# Revit family: led-e-g45-fila-e27-2_8w-dim-2700k-fr_500010000800_a218
name_source: partatom
category: Leuchten
revit_build: Autodesk Revit 2016 (Build: 20190508_0715(x64)
units: mm (PartAtom-declared; Revit-internal decimal feet)

## family parameters
Basisbauteil = Fläche
Beim Laden mit Abzugskörper schneiden = Nein
Bemaßung runder Anschluss = Durchmesser verwenden
Gemeinsam genutzt = Nein
Lichtquelle = Nein
Raumberechnungspunkt = Nein
Teiletyp = Normal

## types (1)
- LED-E-G45-FILA-E27-2.8W-DIM-2700K-FR (1 x LED, 235 lm)
    Approval mark = CE
    Beschreibung = Classic light bulb shape ensures an easy replacement. Instant 100% light when switched on and no startup time. No UV / IR radiance so there is less risk of damage. Up to 86% less energy consumption than traditional bulbs.
    CIE Flux Codes = 21 45 72 54 99
    Height = 77 mm
    Hersteller = OPPLE
    Lamp Light Flux = 235 lm
    Lamp count = 1
    Lampe = 1 x LED
    Length = 45 mm
    Luminous efficacy = 83 lm/W
    ModVariant = Nein
    Modell = 500010000800
    Mounting Place = Ceiling
    Mounting Type = Surface mounted
    Number of Poles = 1
    OnlyDefault = Ja
    Power Factor = 1
    Product Name = LED-E-G45-FILA-E27-2.8W-DIM-2700K-FR
    Product group = Filament Mini Globe
    ProductGroupID = 312
    Protection Class = Protection class I
    Protection Degree = IP 20
    RLX_Detail_Level = 1
    RlxData = <blob elided: 15901 chars, md5=775f46ca>
    Scheinlast = 3 VA
    Socket = socket
    Standby Power = 0 W
    System Light Flux = 233 lm
    System Power = 3 W
    Typenbild = 500010000800.jpg
    Typenkommentare = Product without accessories
    URL = http://relux.com
    VarID = ---
    Voltage = 0 V
    Vorgabe-Ansicht = 1800 mm
    Weight = 0.00 kg
    Width = 45 mm

## geometry (parser evidence)
native form markers: Blend x4, Sweep x15
no freeform markers — native parametric forms only
